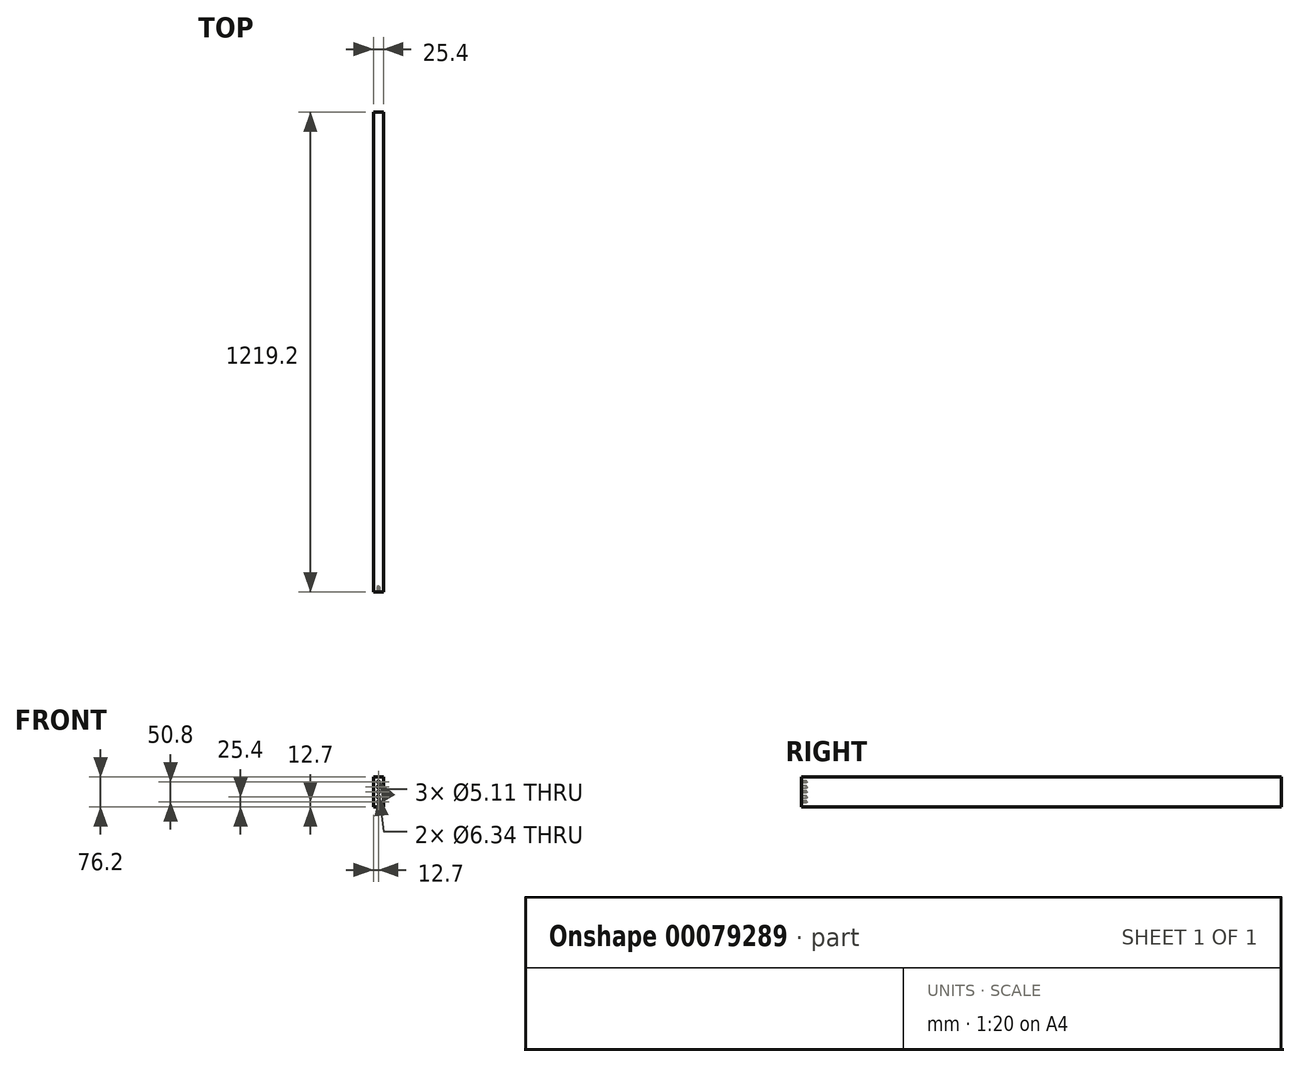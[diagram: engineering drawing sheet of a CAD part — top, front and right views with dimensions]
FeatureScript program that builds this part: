
annotation { "Feature Type Name" : "Feature", "Feature Type Description" : "" }
export const myFeature = defineFeature(function(context is Context, id is Id, definition is map)
    precondition{}
    {
        {
            var Q0;
            Q0=qCreatedBy(makeId("Front.planeOp"),FACE);
            var sketch = newSketch(context, id + "F0", { "sketchPlane" : qUnion([Q0])});
            skLineSegment(sketch, "E0", {"start": v(0, 0) * mm, "end": v(0, 76.2) * mm});
            skLineSegment(sketch, "E1", {"start": v(0, 76.2) * mm, "end": v(25.4, 76.2) * mm});
            skLineSegment(sketch, "E2", {"start": v(25.4, 76.2) * mm, "end": v(25.4, 0) * mm});
            skLineSegment(sketch, "E3", {"start": v(25.4, 0) * mm, "end": v(0, 0) * mm});
            skSolve(sketch);
        }
        {
            var Q0;
            Q0=makeQuery(id+"F0.imprint","IMPRINT",FACE,{"disambiguationData":[TD([[makeQuery(id+"F0.imprint","IMPRINT",EDGE,{"derivedFrom":sQuery(id+"F0.wireOp",EDGE,"E0")}),-1.0]])]});
            extrude(context, id + "F1", {"entities" : qUnion([Q0]), "depth" : 1219.2 * mm});
        }
        {
            var Q0;
            Q0=makeQuery(id+"F1.opExtrude","CAP_FACE",FACE,{"disambiguationData":[OSD([sQuery(id+"F0.wireOp",EDGE,"E0"),sQuery(id+"F0.wireOp",EDGE,"E1"),sQuery(id+"F0.wireOp",EDGE,"E2"),sQuery(id+"F0.wireOp",EDGE,"E3")])],"isStart":false});
            var sketch = newSketch(context, id + "F2", { "sketchPlane" : qUnion([Q0])});
            skPoint(sketch, "E4", {"position": v(12.7, 63.5) * mm});
            skPoint(sketch, "E5", {"position": v(12.7, 50.8) * mm});
            skPoint(sketch, "E6", {"position": v(12.7, 25.4) * mm});
            skPoint(sketch, "E7", {"position": v(12.7, 12.7) * mm});
            skPoint(sketch, "E8", {"position": v(12.7, 38.1) * mm});
            skSolve(sketch);
        }
        {
            var Q0;
            Q0=sQuery(id+"F2.wireOp",VERTEX,"E4");
            var Q1;
            Q1=sQuery(id+"F2.wireOp",VERTEX,"E8");
            var Q2;
            Q2=sQuery(id+"F2.wireOp",VERTEX,"E7");
            var Q3;
            Q3=makeQuery(id+"F1.opExtrude","SWEPT_BODY",BODY,{"disambiguationData":[OSD([sQuery(id+"F0.wireOp",EDGE,"E0"),sQuery(id+"F0.wireOp",EDGE,"E1"),sQuery(id+"F0.wireOp",EDGE,"E2"),sQuery(id+"F0.wireOp",EDGE,"E3")])]});
            hole(context, id + "F3", {"style" : HoleStyle.SIMPLE, "endStyle" : HoleEndStyle.BLIND, "standardTappedOrClearance" : lookupTablePath({ "standard" : "ANSI", "engagement" : "75%", "pitch" : "20 tpi", "size" : "1/4", "type" : "Tapped" }), "standardBlindInLast" : lookupTablePath({ "standard" : "ANSI", "engagement" : "75%", "pitch" : "20 tpi", "size" : "1/4", "type" : "Tapped" }), "holeDiameter" : 5.1 * mm, "holeDepth" : 12.7 * mm, "locations" : qUnion([Q0, Q1, Q2]), "scope" : qUnion([Q3]), "majorDiameter" : 6.35 * mm});
        }
        {
            var Q0;
            Q0=sQuery(id+"F2.wireOp",VERTEX,"E5");
            var Q1;
            Q1=sQuery(id+"F2.wireOp",VERTEX,"E6");
            var Q2;
            Q2=makeQuery(id+"F1.opExtrude","SWEPT_BODY",BODY,{"disambiguationData":[OSD([sQuery(id+"F0.wireOp",EDGE,"E0"),sQuery(id+"F0.wireOp",EDGE,"E1"),sQuery(id+"F0.wireOp",EDGE,"E2"),sQuery(id+"F0.wireOp",EDGE,"E3")])]});
            hole(context, id + "F4", {"style" : HoleStyle.SIMPLE, "endStyle" : HoleEndStyle.BLIND, "holeDiameter" : 6.34 * mm, "holeDepth" : 12.7 * mm, "locations" : qUnion([Q0, Q1]), "scope" : qUnion([Q2])});
        }
    });
